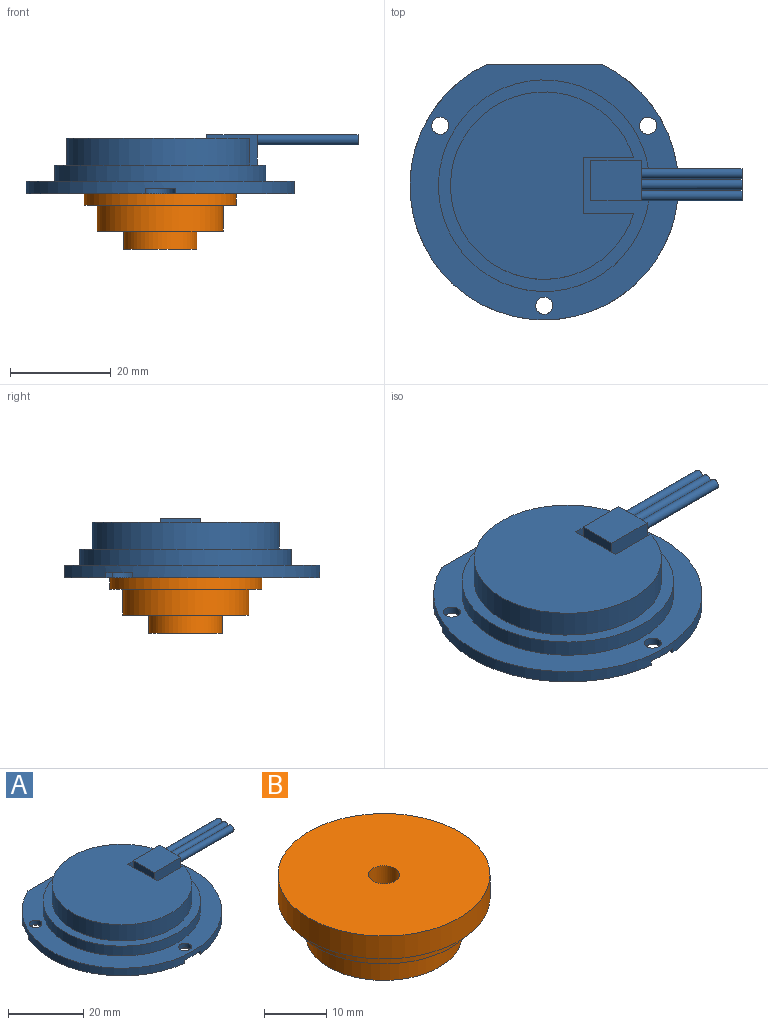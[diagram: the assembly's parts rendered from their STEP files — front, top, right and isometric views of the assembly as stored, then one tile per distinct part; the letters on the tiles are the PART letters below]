
ASSEMBLY  parts=2 mates=1
PART A: 42 faces, bbox 65.9x50.8x11.7 mm
  f0: cylinder r=26.65mm len=53.3mm, axis (0,0,1), area 342.4mm2, adj f5,f6,f7,f26,f28,f29,f30,f32
  f1: cylinder r=1.7mm len=3.4mm, axis (0,0,1), area 16mm2, adj f7,f37
  f2: cylinder r=1.7mm len=3.4mm, axis (0,0,1), area 16mm2, adj f7,f33
  f3: cylinder r=1.7mm len=3.4mm, axis (0,0,1), area 16mm2, adj f7,f29
  f4: plane 1x1mm, normal (1,0,0), area 0.2mm2, adj f18,f19,f20
  f5: plane 22.54x2.5mm, normal (0,1,0), area 56.3mm2, adj f0,f6,f7
  f6: plane 53.3x50.63mm, normal (0,0,-1), area 1138.9mm2, adj f0,f5,f26,f27,f28,f30,f31,f32
  f7: plane 53.3x50.8mm, normal (0,0,1), area 780.6mm2, adj f0,f1,f2,f3,f5,f8
  f8: cylinder r=21mm len=42mm, axis (0,0,-1), area 422.2mm2, adj f7,f9
  f9: plane 42x42mm, normal (0,0,1), area 334.7mm2, adj f8,f10,f11,f12,f13,f15,f16,f17
  f10: plane 10x5.3mm, normal (0,-1,0), area 53mm2, adj f9,f11,f13,f14
  f11: cylinder r=18.6mm len=37.2mm, axis (0,0,-1), area 560.2mm2, adj f9,f10,f12,f14
  f12: plane 10x5.3mm, normal (0,1,0), area 53mm2, adj f9,f11,f13,f14
  f13: plane 11x5.3mm, normal (1,0,0), area 58.3mm2, adj f9,f10,f12,f14
  f14: plane 37.2x36.37mm, normal (0,0,1), area 970.7mm2, adj f10,f11,f12,f13
  f15: plane 8x6mm, normal (1,0,0), area 38.4mm2, adj f9,f16,f18,f19,f20,f22,f24
  f16: plane 10x6mm, normal (0,1,0), area 60mm2, adj f9,f15,f17,f19
  f17: plane 8x6mm, normal (-1,0,0), area 48mm2, adj f9,f16,f18,f19
  f18: plane 10x6mm, normal (0,-1,0), area 60mm2, adj f4,f9,f15,f17,f19
  f19: plane 10x8mm, normal (0,0,1), area 80mm2, adj f4,f15,f16,f17,f18
  f20: cylinder r=1mm len=20mm, axis (-1,0,0), area 125.7mm2, adj f4,f15,f21
  f21: plane 2x2mm, normal (1,0,0), area 3.1mm2, adj f20
  f22: cylinder r=1mm len=20mm, axis (-1,0,0), area 125.7mm2, adj f15,f23
  f23: plane 2x2mm, normal (1,0,0), area 3.1mm2, adj f22
  f24: cylinder r=1mm len=20mm, axis (-1,0,0), area 125.7mm2, adj f15,f25
  f25: plane 2x2mm, normal (1,0,0), area 3.1mm2, adj f24
  f26: plane 2.66x1mm, normal (1,0,0), area 2.7mm2, adj f0,f6,f27,f29
  f27: cylinder r=3mm len=6mm, axis (0,0,-1), area 9.4mm2, adj f6,f26,f28,f29
  f28: plane 2.66x1mm, normal (-1,0,0), area 2.7mm2, adj f0,f6,f27,f29
  f29: plane 6x5.83mm, normal (0,0,-1), area 21.7mm2, adj f0,f3,f26,f27,f28
  f30: plane 2.3x1.33mm, normal (-0.5,0.87,0), area 2.7mm2, adj f0,f6,f31,f33
  f31: cylinder r=3mm len=5.6mm, axis (0,0,-1), area 9.4mm2, adj f6,f30,f32,f33
  f32: plane 2.3x1.33mm, normal (0.5,-0.87,0), area 2.7mm2, adj f0,f6,f31,f33
  f33: plane 6.93x6.8mm, normal (0,0,-1), area 21.7mm2, adj f0,f2,f30,f31,f32
  f34: plane 2.3x1.33mm, normal (-0.5,-0.87,0), area 2.7mm2, adj f0,f6,f35,f37
  f35: cylinder r=3mm len=5.6mm, axis (0,0,-1), area 9.4mm2, adj f6,f34,f36,f37
  f36: plane 2.3x1.33mm, normal (0.5,0.87,0), area 2.7mm2, adj f0,f6,f35,f37
  f37: plane 6.93x6.8mm, normal (0,0,-1), area 21.7mm2, adj f0,f1,f34,f35,f36
  f38: cylinder r=2.5mm len=5mm, axis (0,0,-1), area 78.5mm2, adj f40,f41
  f39: cylinder r=17.5mm len=35mm, axis (0,0,-1), area 549.8mm2, adj f6,f40
  f40: plane 35x35mm, normal (0,0,-1), area 942.5mm2, adj f38,f39
  f41: plane 5x5mm, normal (0,0,-1), area 19.6mm2, adj f38
PART B: 29 faces, bbox 34x34x15.5 mm
  f0: cylinder r=1.03mm len=6.85mm, axis (0,0,-1), area 44.1mm2, adj f1,f2
  f1: cone r=1.03mm half-angle=45deg, axis (0,0,-1), area 5.7mm2, adj f0,f21
  f2: cone r=0mm half-angle=59deg, axis (0,0,-1), area 3.9mm2, adj f0
  f3: cylinder r=1.03mm len=6.85mm, axis (0,0,-1), area 44.1mm2, adj f4,f5
  f4: cone r=1.03mm half-angle=45deg, axis (0,0,-1), area 5.7mm2, adj f3,f21
  f5: cone r=0mm half-angle=59deg, axis (0,0,-1), area 3.9mm2, adj f3
  f6: cylinder r=1.03mm len=6.85mm, axis (0,0,-1), area 44.1mm2, adj f7,f8
  f7: cone r=1.03mm half-angle=45deg, axis (0,0,-1), area 5.7mm2, adj f6,f21
  f8: cone r=0mm half-angle=59deg, axis (0,0,-1), area 3.9mm2, adj f6
  f9: cylinder r=1.03mm len=6.85mm, axis (0,0,-1), area 44.1mm2, adj f10,f11
  f10: cone r=1.03mm half-angle=45deg, axis (0,0,-1), area 5.7mm2, adj f9,f21
  f11: cone r=0mm half-angle=59deg, axis (0,0,-1), area 3.9mm2, adj f9
  f12: cylinder r=1.03mm len=6.85mm, axis (0,0,-1), area 44.1mm2, adj f13,f14
  f13: cone r=1.03mm half-angle=45deg, axis (0,0,-1), area 5.7mm2, adj f12,f21
  f14: cone r=0mm half-angle=59deg, axis (0,0,-1), area 3.9mm2, adj f12
  f15: cylinder r=17mm len=34mm, axis (0,0,1), area 480.7mm2, adj f16,f17
  f16: plane 34x34mm, normal (0,0,-1), area 191.6mm2, adj f15,f18
  f17: plane 34x34mm, normal (0,0,1), area 888.2mm2, adj f15,f24
  f18: cylinder r=15.1mm len=30.2mm, axis (0,0,1), area 218.2mm2, adj f16,f19
  f19: plane 30.2x30.2mm, normal (0,0,-1), area 225.4mm2, adj f18,f20
  f20: cylinder r=12.5mm len=25mm, axis (0,0,1), area 400.6mm2, adj f19,f21
  f21: plane 25x25mm, normal (0,0,-1), area 279.6mm2, adj f1,f4,f7,f10,f13,f20,f23,f27
  f22: plane 14.6x14.6mm, normal (0,0,-1), area 167.4mm2, adj f23
  f23: cylinder r=7.3mm len=14.6mm, axis (0,0,1), area 165.1mm2, adj f21,f22
  f24: cylinder r=2.5mm len=5.01mm, axis (0,0,1), area 70.8mm2, adj f17,f25
  f25: plane 5.01x5.01mm, normal (0,0,1), area 19.7mm2, adj f24
  f26: cylinder r=1.03mm len=6.85mm, axis (0,0,-1), area 44.1mm2, adj f27,f28
  f27: cone r=1.03mm half-angle=45deg, axis (0,0,-1), area 5.7mm2, adj f21,f26
  f28: cone r=0mm half-angle=59deg, axis (0,0,-1), area 3.9mm2, adj f26
PLACE A at identity fixed
PLACE B rot(axis=(0,0,-1),68.9deg) t=(0,0,0)mm
MATE revolute B.f24 <-> A.f38  axis (0,0,1) through (0,0,-2.5)mm
